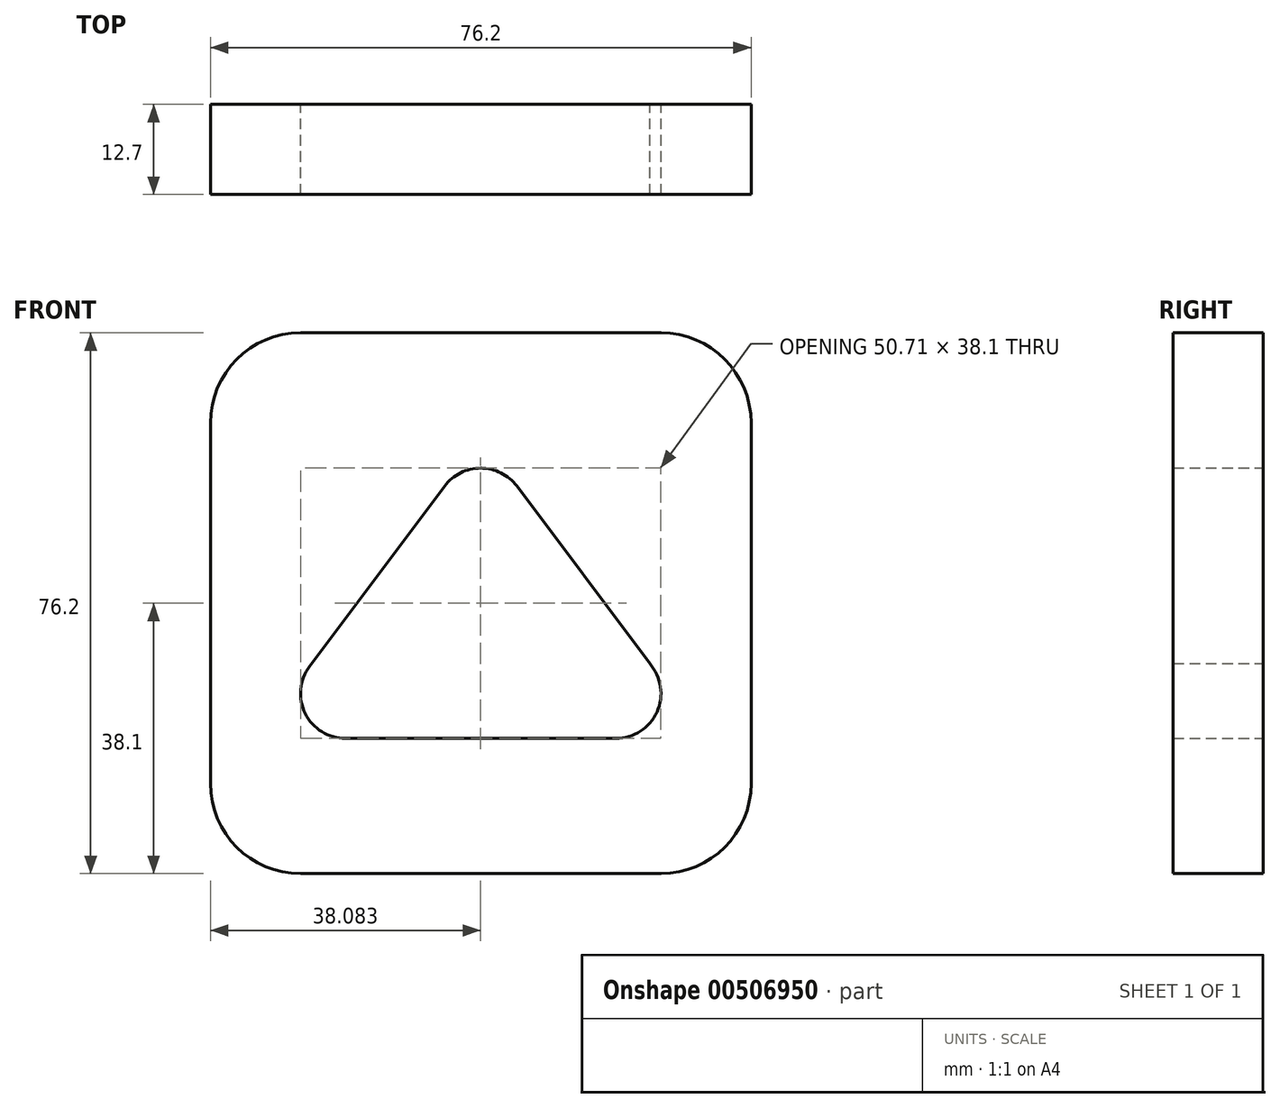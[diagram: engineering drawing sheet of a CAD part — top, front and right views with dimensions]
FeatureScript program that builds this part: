
annotation { "Feature Type Name" : "Feature", "Feature Type Description" : "" }
export const myFeature = defineFeature(function(context is Context, id is Id, definition is map)
    precondition{}
    {
        {
            var Q0;
            Q0=qCreatedBy(makeId("Front.planeOp"),FACE);
            var sketch = newSketch(context, id + "F0", { "sketchPlane" : qUnion([Q0])});
            skLineSegment(sketch, "E0", {"start": v(12.7, 0) * mm, "end": v(63.5, 0) * mm});
            skLineSegment(sketch, "E1", {"start": v(76.2, 12.7) * mm, "end": v(76.2, 63.5) * mm});
            skLineSegment(sketch, "E2", {"start": v(63.5, 76.2) * mm, "end": v(12.7, 76.2) * mm});
            skLineSegment(sketch, "E3", {"start": v(0, 63.5) * mm, "end": v(0, 12.7) * mm});
            skArc(sketch, "E4", {"start": v(13.97, 29.21) * mm, "mid": v(13.37, 22.56) * mm, "end": v(19.05, 19.05) * mm});
            skArc(sketch, "E5", {"start": v(57.15, 19.05) * mm, "mid": v(62.94, 22.79) * mm, "end": v(61.91, 29.6) * mm});
            skArc(sketch, "E6", {"start": v(43.18, 54.6) * mm, "mid": v(38.1, 57.15) * mm, "end": v(33.02, 54.6) * mm});
            skLineSegment(sketch, "E7", {"start": v(33.02, 54.6) * mm, "end": v(13.97, 29.21) * mm});
            skLineSegment(sketch, "E8", {"start": v(19.05, 19.05) * mm, "end": v(57.15, 19.05) * mm});
            skLineSegment(sketch, "E9", {"start": v(62.52, 28.8) * mm, "end": v(43.18, 54.6) * mm});
            skArc(sketch, "E10", {"start": v(12.7, 76.2) * mm, "mid": v(3.72, 72.48) * mm, "end": v(0, 63.5) * mm});
            skArc(sketch, "E11", {"start": v(76.2, 63.5) * mm, "mid": v(72.48, 72.48) * mm, "end": v(63.5, 76.2) * mm});
            skArc(sketch, "E12", {"start": v(0, 12.7) * mm, "mid": v(3.72, 3.72) * mm, "end": v(12.7, 0) * mm});
            skPoint(sketch, "E13.visualSharp", {"position": v(76.2, 0) * mm});
            skArc(sketch, "E13.filletArc", {"start": v(63.5, 0) * mm, "mid": v(72.48, 3.72) * mm, "end": v(76.2, 12.7) * mm});
            skSolve(sketch);
        }
        {
            var Q0;
            Q0=makeQuery(id+"F0.imprint","IMPRINT",FACE,{"disambiguationData":[TD([[makeQuery(id+"F0.imprint","IMPRINT",EDGE,{"derivedFrom":sQuery(id+"F0.wireOp",EDGE,"E0")}),1.0]])]});
            extrude(context, id + "F1", {"entities" : qUnion([Q0]), "depth" : 12.7 * mm});
        }
    });
